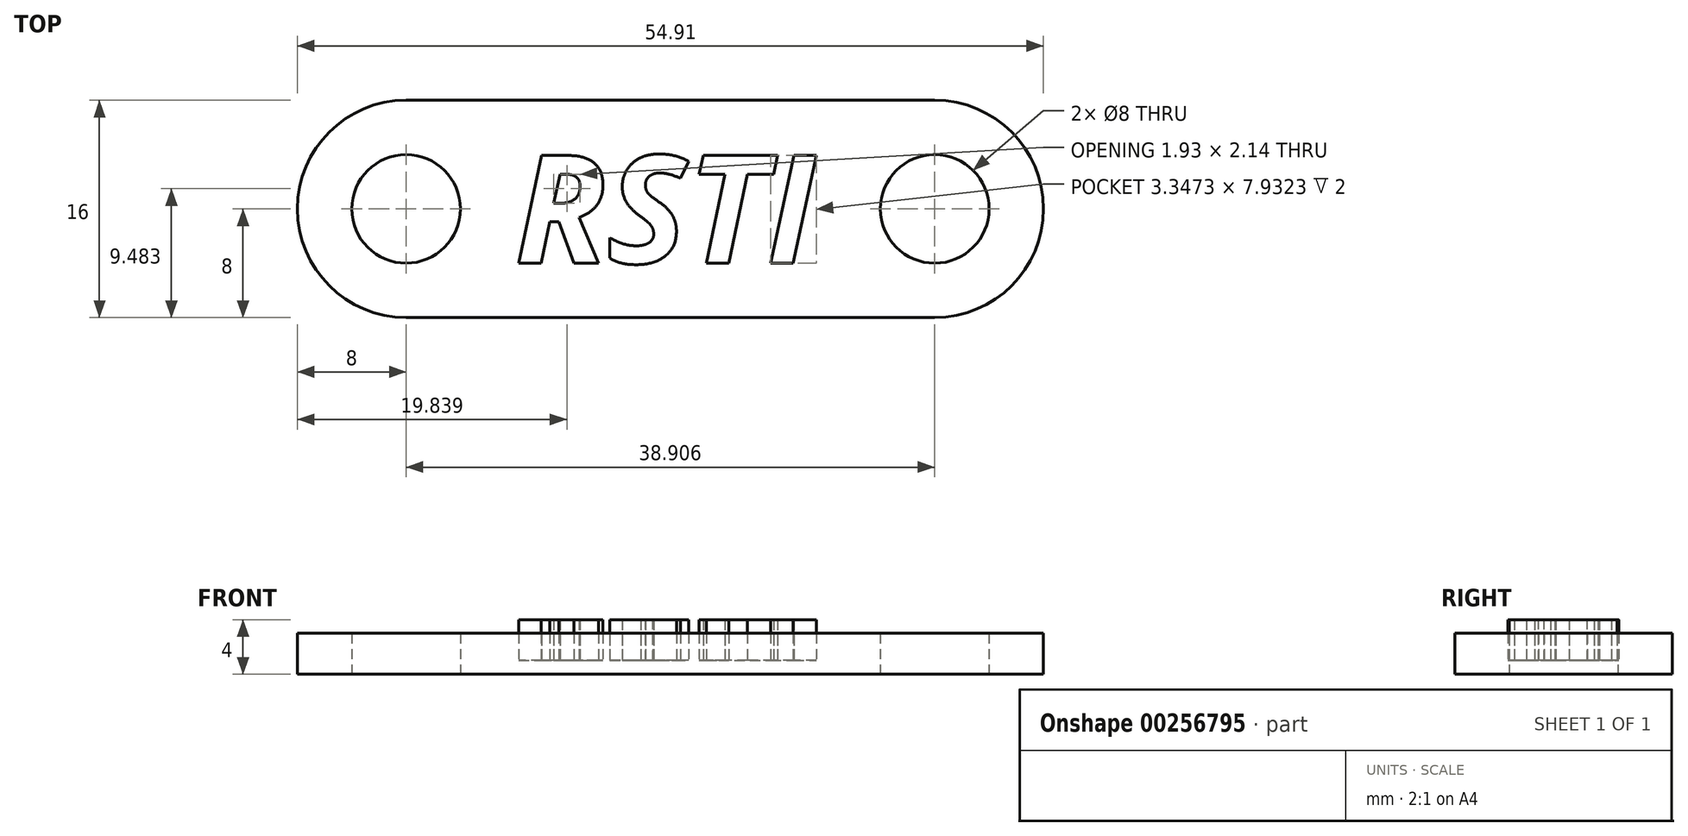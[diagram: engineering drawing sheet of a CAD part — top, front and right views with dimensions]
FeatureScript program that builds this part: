
annotation { "Feature Type Name" : "Feature", "Feature Type Description" : "" }
export const myFeature = defineFeature(function(context is Context, id is Id, definition is map)
    precondition{}
    {
        {
            var Q0;
            Q0=qCreatedBy(makeId("Top.planeOp"),FACE);
            cPlane(context, id + "F0", {"entities" : qUnion([Q0]), "cplaneType" : CPlaneType.OFFSET, "offset" : 1 * mm, "width" : 152.4 * mm, "height" : 152.4 * mm});
        }
        {
            var Q0;
            Q0=qCreatedBy(id+"F0.planeOp",FACE);
            var sketch = newSketch(context, id + "F1", { "sketchPlane" : qUnion([Q0])});
            skText(sketch, "E0", { "text": "RSTI", "fontName": "OpenSans-BoldItalic.ttf"});
            const initialGuessF1  = {"E0": [0, 0, 1, 0, 0.008]};
            skSetInitialGuess(sketch, initialGuessF1);
            skSolve(sketch);
        }
        {
            var Q0;
            Q0=qCreatedBy(makeId("Top.planeOp"),FACE);
            var sketch = newSketch(context, id + "F2", { "sketchPlane" : qUnion([Q0])});
            skLineSegment(sketch, "E1.0", {"start": v(0, 0) * mm, "end": v(0, 4) * mm, "construction": true});
            skLineSegment(sketch, "E2.0", {"start": v(0, 8) * mm, "end": v(22.9, 8) * mm, "construction": true});
            skLineSegment(sketch, "E3.0", {"start": v(22.9, 0) * mm, "end": v(22.9, 0) * mm});
            skLineSegment(sketch, "E4.0", {"start": v(0, 0) * mm, "end": v(11.45, 0) * mm, "construction": true});
            skLineSegment(sketch, "E5.0", {"start": v(11.45, 0) * mm, "end": v(11.45, 4) * mm, "construction": true});
            skLineSegment(sketch, "E6", {"start": v(11.45, 4) * mm, "end": v(11.45, 8) * mm, "construction": true});
            skLineSegment(sketch, "E7", {"start": v(0, 4) * mm, "end": v(0, 8) * mm, "construction": true});
            skLineSegment(sketch, "E8", {"start": v(0, 8) * mm, "end": v(0, 8) * mm});
            skLineSegment(sketch, "E9", {"start": v(22.9, 8) * mm, "end": v(22.9, 8) * mm});
            skLineSegment(sketch, "E10", {"start": v(22.9, 0) * mm, "end": v(22.9, 4) * mm, "construction": true});
            skLineSegment(sketch, "E11", {"start": v(11.45, 0) * mm, "end": v(22.9, 0) * mm, "construction": true});
            skLineSegment(sketch, "E12", {"start": v(22.9, 4) * mm, "end": v(22.9, 8) * mm, "construction": true});
            skLineSegment(sketch, "E13", {"start": v(0, 4) * mm, "end": v(-8, 4) * mm, "construction": true});
            skCircle(sketch, "E14", {"center": v(-8, 4) * mm, "radius": 8 * mm});
            skLineSegment(sketch, "E15", {"start": v(-8, 4) * mm, "end": v(-8, 8) * mm});
            skLineSegment(sketch, "E16", {"start": v(-8, 8) * mm, "end": v(-8, 12) * mm});
            skCircle(sketch, "E17", {"center": v(-8, 4) * mm, "radius": 4 * mm});
            skLineSegment(sketch, "E18.MirrorCS", {"start": v(-8, 4) * mm, "end": v(-8, 0) * mm});
            skLineSegment(sketch, "E19.MirrorCS", {"start": v(-8, 0) * mm, "end": v(-8, -4) * mm});
            skCircle(sketch, "E20.MirrorC", {"center": v(30.9, 4) * mm, "radius": 8 * mm});
            skCircle(sketch, "E21.MirrorC", {"center": v(30.9, 4) * mm, "radius": 4 * mm});
            skLineSegment(sketch, "E22.MirrorCS", {"start": v(22.9, 4) * mm, "end": v(30.9, 4) * mm, "construction": true});
            skLineSegment(sketch, "E23.MirrorCS", {"start": v(30.9, 8) * mm, "end": v(30.9, 12) * mm});
            skLineSegment(sketch, "E24.MirrorCS", {"start": v(30.9, 4) * mm, "end": v(30.9, 8) * mm});
            skLineSegment(sketch, "E25.MirrorCS", {"start": v(30.9, 4) * mm, "end": v(30.9, 0) * mm});
            skLineSegment(sketch, "E26.MirrorCS", {"start": v(30.9, 0) * mm, "end": v(30.9, -4) * mm});
            skLineSegment(sketch, "E27", {"start": v(-8, 12) * mm, "end": v(30.9, 12) * mm});
            skLineSegment(sketch, "E28", {"start": v(-8, -4) * mm, "end": v(30.9, -4) * mm});
            skSolve(sketch);
        }
        {
            var Q0;
            Q0 = qSketchRegion(id + "F2", true);
            extrude(context, id + "F3", {"entities" : qUnion([Q0]), "depth" : 3 * mm});
        }
        {
            var Q0;
            Q0 = qSketchRegion(id + "F1", true);
            var Q1;
            Q1=makeQuery(id+"F3.opExtrude","CAP_FACE",FACE,{"disambiguationData":[OSD([sQuery(id+"F2.wireOp",EDGE,"E14"),sQuery(id+"F2.wireOp",EDGE,"E17"),sQuery(id+"F2.wireOp",EDGE,"E20.MirrorC"),sQuery(id+"F2.wireOp",EDGE,"E21.MirrorC"),sQuery(id+"F2.wireOp",EDGE,"E27"),sQuery(id+"F2.wireOp",EDGE,"E28")])],"isStart":false});
            extrude(context, id + "F4", {"entities" : qUnion([Q0]), "operationType" : NewBodyOperationType.REMOVE, "endBound" : BoundingType.UP_TO_SURFACE, "endBoundEntityFace" : qUnion([Q1]), "depth" : 25 * mm});
        }
        {
            var Q0;
            Q0 = qSketchRegion(id + "F1", true);
            extrude(context, id + "F5", {"entities" : qUnion([Q0]), "depth" : 3 * mm});
        }
    });
